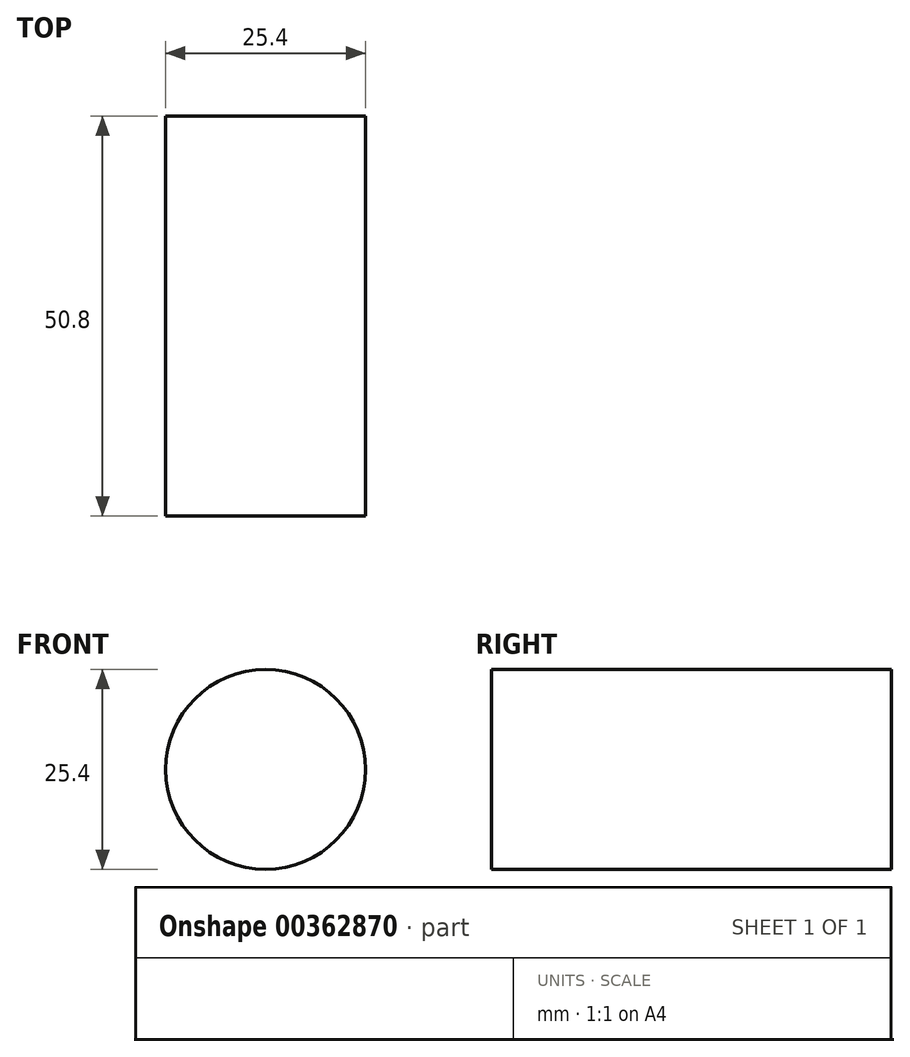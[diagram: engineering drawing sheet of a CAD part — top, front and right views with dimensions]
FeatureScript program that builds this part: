
annotation { "Feature Type Name" : "Feature", "Feature Type Description" : "" }
export const myFeature = defineFeature(function(context is Context, id is Id, definition is map)
    precondition{}
    {
        {
            var Q0;
            Q0=qCreatedBy(makeId("Front.planeOp"),FACE);
            var sketch = newSketch(context, id + "F0", { "sketchPlane" : qUnion([Q0])});
            skCircle(sketch, "E0", {"center": v(0, 0) * mm, "radius": 12.7 * mm});
            skSolve(sketch);
        }
        {
            var Q0;
            Q0=makeQuery(id+"F0.imprint","IMPRINT",FACE,{"disambiguationData":[TD([[makeQuery(id+"F0.imprint","IMPRINT",EDGE,{"derivedFrom":sQuery(id+"F0.wireOp",EDGE,"E0")}),1.0]])]});
            extrude(context, id + "F1", {"entities" : qUnion([Q0]), "depth" : 50.8 * mm});
        }
    });
